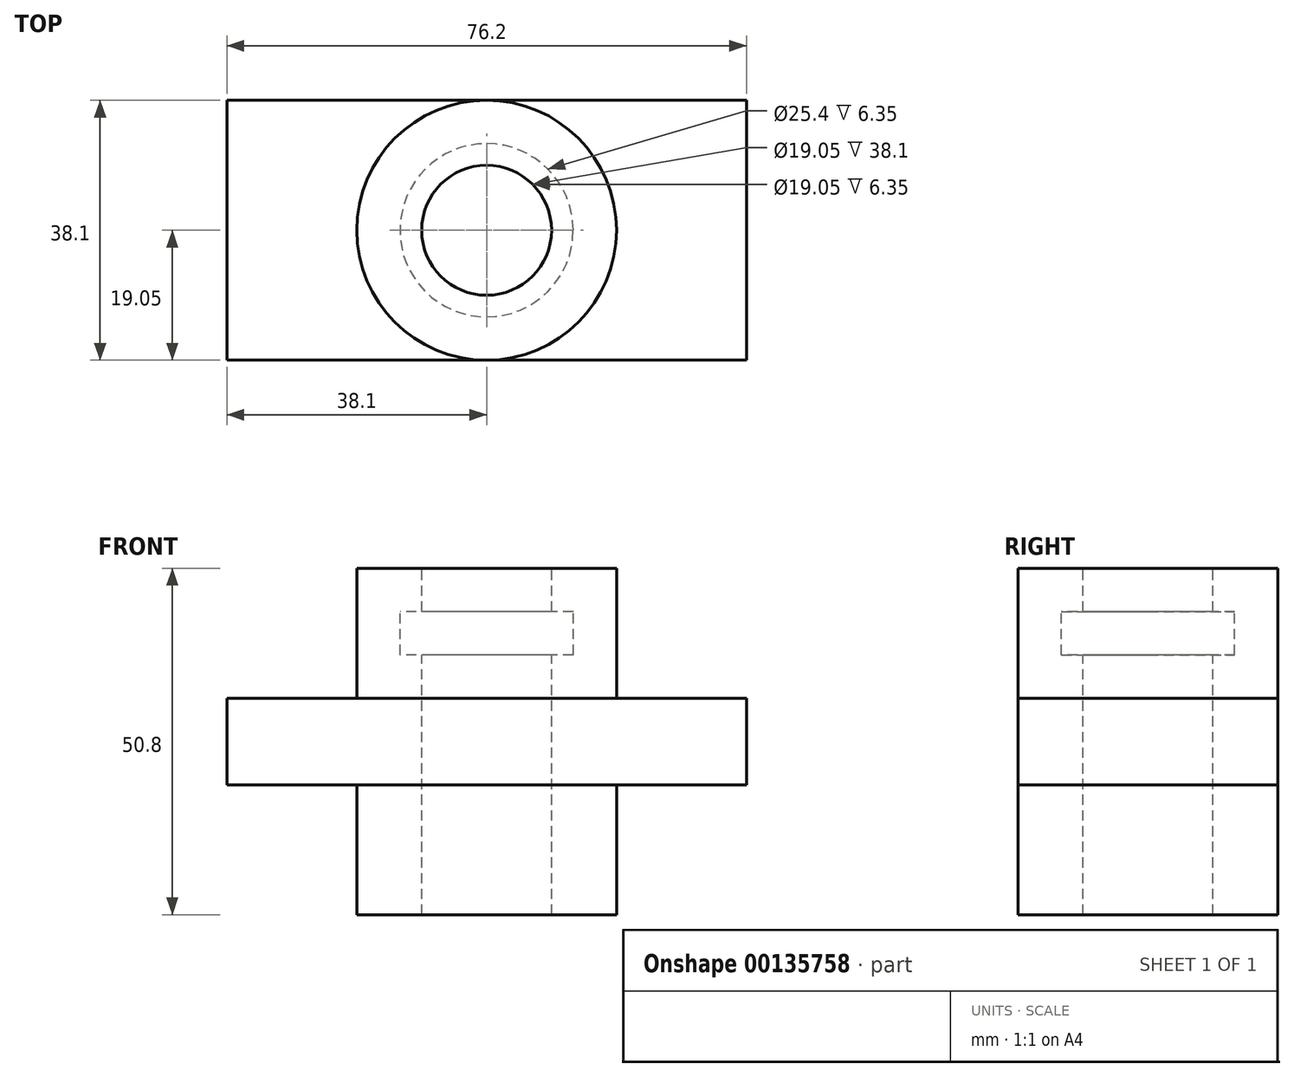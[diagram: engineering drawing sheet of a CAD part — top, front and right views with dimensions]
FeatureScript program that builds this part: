
annotation { "Feature Type Name" : "Feature", "Feature Type Description" : "" }
export const myFeature = defineFeature(function(context is Context, id is Id, definition is map)
    precondition{}
    {
        {
            var Q0;
            Q0=qCreatedBy(makeId("Front.planeOp"),FACE);
            var sketch = newSketch(context, id + "F0", { "sketchPlane" : qUnion([Q0])});
            skLineSegment(sketch, "E0.bottom", {"start": v(0, 0) * mm, "end": v(76.2, 0) * mm});
            skLineSegment(sketch, "E0.top", {"start": v(0, 12.7) * mm, "end": v(76.2, 12.7) * mm});
            skLineSegment(sketch, "E0.left", {"start": v(0, 0) * mm, "end": v(0, 12.7) * mm});
            skLineSegment(sketch, "E0.right", {"start": v(76.2, 0) * mm, "end": v(76.2, 12.7) * mm});
            skSolve(sketch);
        }
        {
            var Q0;
            Q0 = qSketchRegion(id + "F0", true);
            extrude(context, id + "F1", {"entities" : qUnion([Q0]), "oppositeDirection" : true, "depth" : 38.1 * mm});
        }
        {
            var Q0;
            Q0=makeQuery(id+"F1.opExtrude","SWEPT_FACE",FACE,{"disambiguationData":[OSD([sQuery(id+"F0.wireOp",EDGE,"E0.top")])]});
            var sketch = newSketch(context, id + "F2", { "sketchPlane" : qUnion([Q0])});
            skCircle(sketch, "E1", {"center": v(38.1, 19.05) * mm, "radius": 19.05 * mm});
            skPoint(sketch, "E1.centerSnap0", {"position": v(0, 19.05) * mm});
            skPoint(sketch, "E1.centerSnap1", {"position": v(38.1, 38.1) * mm});
            skSolve(sketch);
        }
        {
            var Q0;
            Q0=makeQuery(id+"F1.opExtrude","SWEPT_FACE",FACE,{"disambiguationData":[OSD([sQuery(id+"F0.wireOp",EDGE,"E0.bottom")])]});
            var sketch = newSketch(context, id + "F3", { "sketchPlane" : qUnion([Q0])});
            skCircle(sketch, "E2", {"center": v(38.1, -19.05) * mm, "radius": 19.05 * mm});
            skPoint(sketch, "E2.centerSnap0", {"position": v(0, -19.05) * mm});
            skPoint(sketch, "E2.centerSnap1", {"position": v(38.1, 0) * mm});
            skSolve(sketch);
        }
        {
            var Q0;
            {var subQ0=sQuery(id+"F2.wireOp",EDGE,"E1");var subQ1=sQuery(id+"F0.wireOp",EDGE,"E0.top");var subQ2=makeQuery(id+"F2.imprint","INTERSECT",VERTEX,{"derivedFrom":[makeQuery(id+"F1.opExtrude","CAP_EDGE",EDGE,{"disambiguationData":[OSD([subQ1])],"isStart":true}),subQ0]});Q0=makeQuery(id+"F2.imprint","IMPRINT",FACE,{"disambiguationData":[TD([[makeQuery(id+"F2.imprint","IMPRINT",EDGE,{"disambiguationData":[TD([[subQ2,1.0]])],"derivedFrom":subQ0}),1.0]])]});}
            extrude(context, id + "F4", {"entities" : qUnion([Q0]), "operationType" : NewBodyOperationType.ADD, "depth" : 19.05 * mm});
        }
        {
            var Q0;
            {var subQ0=sQuery(id+"F3.wireOp",EDGE,"E2");var subQ1=sQuery(id+"F0.wireOp",EDGE,"E0.bottom");var subQ2=makeQuery(id+"F3.imprint","INTERSECT",VERTEX,{"derivedFrom":[makeQuery(id+"F1.opExtrude","CAP_EDGE",EDGE,{"disambiguationData":[OSD([subQ1])],"isStart":true}),subQ0]});Q0=makeQuery(id+"F3.imprint","IMPRINT",FACE,{"disambiguationData":[TD([[makeQuery(id+"F3.imprint","IMPRINT",EDGE,{"disambiguationData":[TD([[subQ2,-1.0]])],"derivedFrom":subQ0}),1.0]])]});}
            extrude(context, id + "F5", {"entities" : qUnion([Q0]), "operationType" : NewBodyOperationType.ADD, "depth" : 19.05 * mm});
        }
        {
            var Q0;
            Q0=makeQuery(id+"F4.opExtrude","CAP_FACE",FACE,{"disambiguationData":[OSD([sQuery(id+"F2.wireOp",EDGE,"E1")])],"isStart":false});
            var sketch = newSketch(context, id + "F6", { "sketchPlane" : qUnion([Q0])});
            skCircle(sketch, "E3", {"center": v(38.1, 19.05) * mm, "radius": 9.53 * mm});
            skSolve(sketch);
        }
        {
            var Q0;
            Q0=makeQuery(id+"F6.imprint","IMPRINT",FACE,{"disambiguationData":[TD([[makeQuery(id+"F6.imprint","IMPRINT",EDGE,{"derivedFrom":sQuery(id+"F6.wireOp",EDGE,"E3")}),1.0]])]});
            extrude(context, id + "F7", {"entities" : qUnion([Q0]), "operationType" : NewBodyOperationType.REMOVE, "oppositeDirection" : true, "depth" : 127 * mm});
        }
        {
            var Q0;
            Q0=makeQuery(id+"F4.opExtrude","CAP_FACE",FACE,{"disambiguationData":[OSD([sQuery(id+"F2.wireOp",EDGE,"E1")])],"isStart":false});
            var sketch = newSketch(context, id + "F8", { "sketchPlane" : qUnion([Q0])});
            skCircle(sketch, "E4", {"center": v(38.1, 19.05) * mm, "radius": 12.7 * mm});
            skSolve(sketch);
        }
        {
            var Q0;
            Q0=makeQuery(id+"F8.imprint","IMPRINT",FACE,{"disambiguationData":[TD([[makeQuery(id+"F8.imprint","IMPRINT",EDGE,{"derivedFrom":sQuery(id+"F8.wireOp",EDGE,"E4")}),1.0]])]});
            extrude(context, id + "F9", {"entities" : qUnion([Q0]), "operationType" : NewBodyOperationType.REMOVE, "oppositeDirection" : true, "depth" : 12.7 * mm});
        }
        {
            var Q0;
            Q0=makeQuery(id+"F4.opExtrude","CAP_FACE",FACE,{"disambiguationData":[OSD([sQuery(id+"F2.wireOp",EDGE,"E1")])],"isStart":false});
            var sketch = newSketch(context, id + "F10", { "sketchPlane" : qUnion([Q0])});
            skCircle(sketch, "E5", {"center": v(38.1, 19.05) * mm, "radius": 12.7 * mm});
            skCircle(sketch, "E6", {"center": v(38.1, 19.05) * mm, "radius": 9.53 * mm});
            skSolve(sketch);
        }
        {
            var Q0;
            Q0=makeQuery(id+"F10.imprint","IMPRINT",FACE,{"disambiguationData":[TD([[makeQuery(id+"F10.imprint","IMPRINT",EDGE,{"derivedFrom":sQuery(id+"F10.wireOp",EDGE,"E5")}),1.0]])]});
            extrude(context, id + "F11", {"entities" : qUnion([Q0]), "operationType" : NewBodyOperationType.ADD, "oppositeDirection" : true, "depth" : 6.35 * mm});
        }
    });
